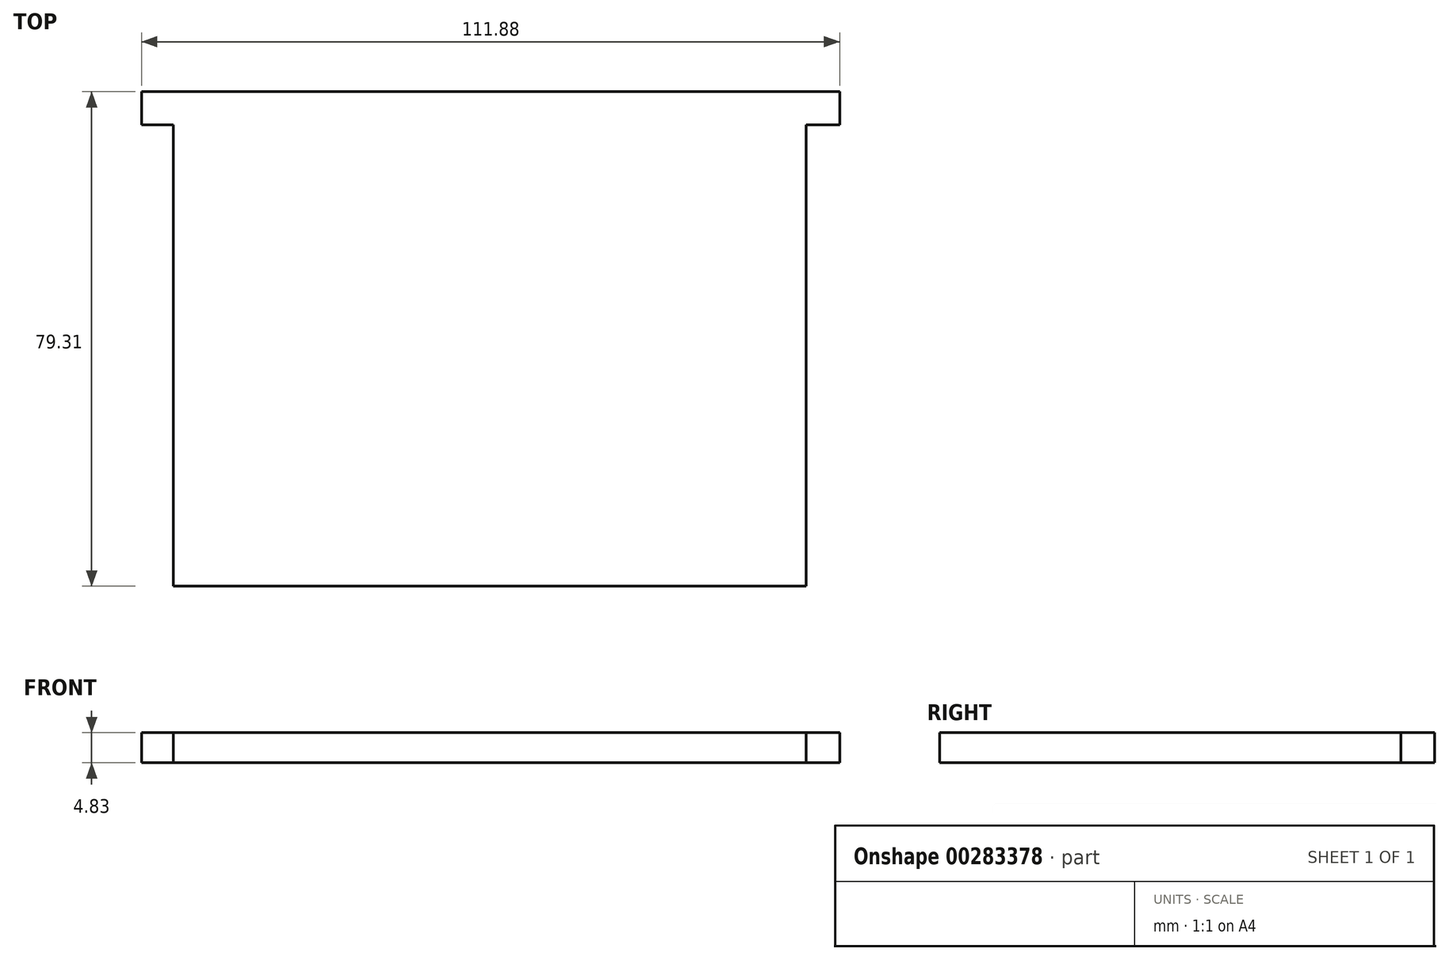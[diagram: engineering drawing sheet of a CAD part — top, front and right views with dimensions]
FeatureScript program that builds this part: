
annotation { "Feature Type Name" : "Feature", "Feature Type Description" : "" }
export const myFeature = defineFeature(function(context is Context, id is Id, definition is map)
    precondition{}
    {
        {
            var Q0;
            Q0=qCreatedBy(makeId("Top.planeOp"),FACE);
            var sketch = newSketch(context, id + "F0", { "sketchPlane" : qUnion([Q0])});
            skLineSegment(sketch, "E0", {"start": v(-38.84, 39.77) * mm, "end": v(-38.84, -39.54) * mm});
            skLineSegment(sketch, "E1", {"start": v(-38.84, 39.77) * mm, "end": v(62.57, 39.77) * mm});
            skLineSegment(sketch, "E2", {"start": v(-38.84, -39.54) * mm, "end": v(62.57, -39.54) * mm});
            skLineSegment(sketch, "E3", {"start": v(62.57, 39.77) * mm, "end": v(62.57, -39.54) * mm});
            skLineSegment(sketch, "E4", {"start": v(-38.84, 39.77) * mm, "end": v(-43.96, 39.77) * mm});
            skLineSegment(sketch, "E5", {"start": v(62.57, 39.77) * mm, "end": v(67.92, 39.77) * mm});
            skLineSegment(sketch, "E6", {"start": v(-43.96, 39.77) * mm, "end": v(-43.96, 34.42) * mm});
            skLineSegment(sketch, "E7", {"start": v(-43.96, 34.42) * mm, "end": v(-38.84, 34.42) * mm});
            skLineSegment(sketch, "E8", {"start": v(67.92, 39.77) * mm, "end": v(67.92, 34.42) * mm});
            skLineSegment(sketch, "E9", {"start": v(67.92, 34.42) * mm, "end": v(62.57, 34.42) * mm});
            skSolve(sketch);
        }
        {
            var Q0;
            {var subQ1=sQuery(id+"F0.wireOp",EDGE,"E1");Q0=makeQuery(id+"F0.imprint","IMPRINT",FACE,{"disambiguationData":[TD([[makeQuery(id+"F0.imprint","IMPRINT",EDGE,{"derivedFrom":subQ1}),-1.0]])]});}
            var Q1;
            {var subQ0=sQuery(id+"F0.wireOp",EDGE,"E4");Q1=makeQuery(id+"F0.imprint","IMPRINT",FACE,{"disambiguationData":[TD([[makeQuery(id+"F0.imprint","IMPRINT",EDGE,{"derivedFrom":subQ0}),1.0]])]});}
            var Q2;
            {var subQ0=sQuery(id+"F0.wireOp",EDGE,"E5");Q2=makeQuery(id+"F0.imprint","IMPRINT",FACE,{"disambiguationData":[TD([[makeQuery(id+"F0.imprint","IMPRINT",EDGE,{"derivedFrom":subQ0}),-1.0]])]});}
            extrude(context, id + "F1", {"entities" : qUnion([Q0, Q1, Q2]), "depth" : 4.83 * mm});
        }
    });
